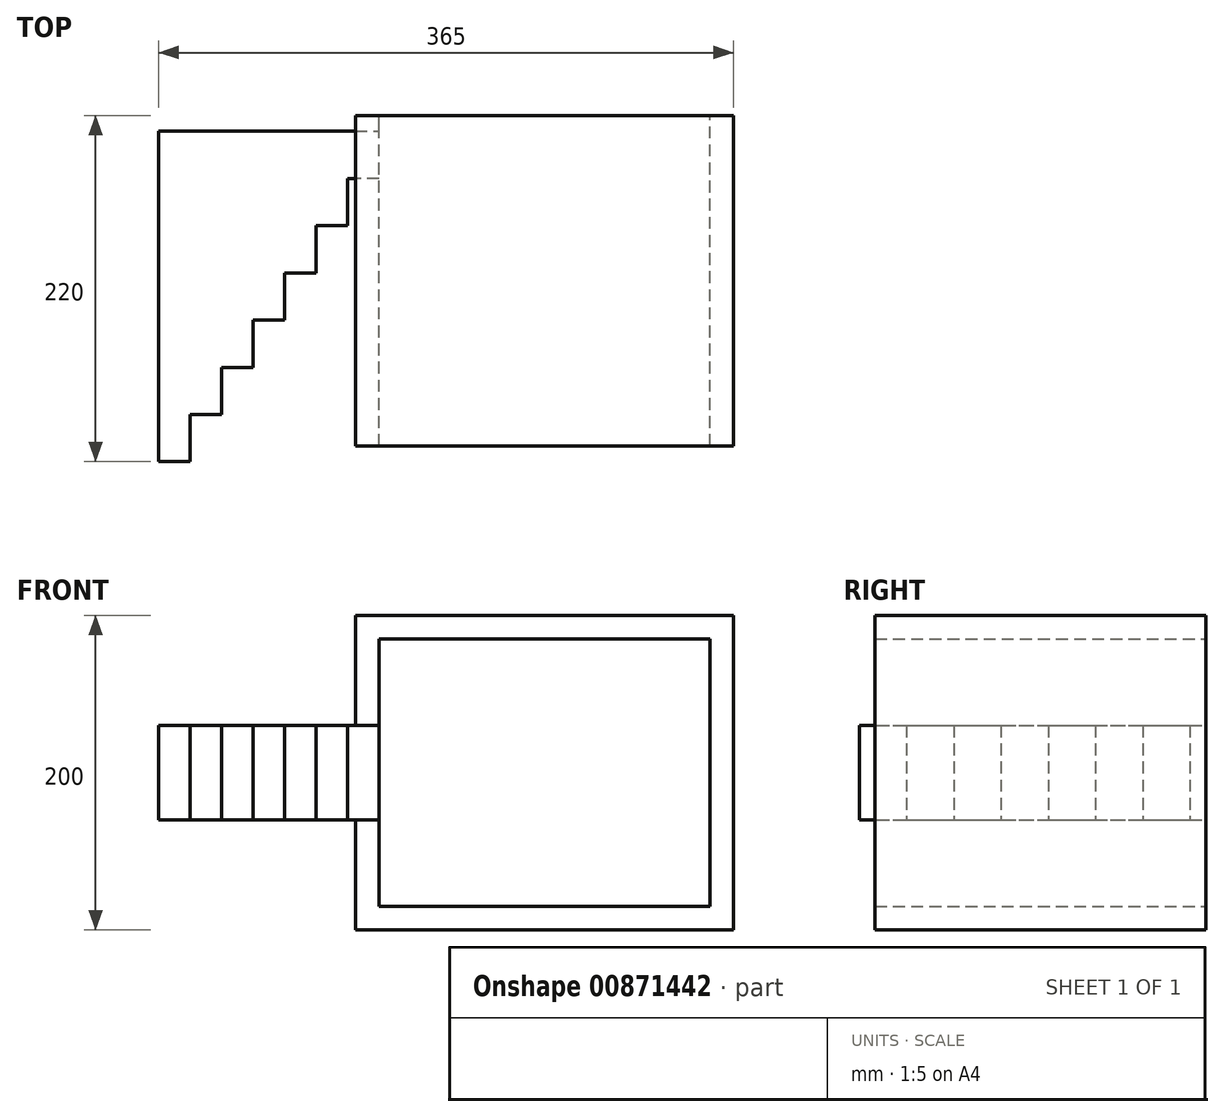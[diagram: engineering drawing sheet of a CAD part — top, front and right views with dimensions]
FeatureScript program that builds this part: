
annotation { "Feature Type Name" : "Feature", "Feature Type Description" : "" }
export const myFeature = defineFeature(function(context is Context, id is Id, definition is map)
    precondition{}
    {
        {
            var Q0;
            Q0=qCreatedBy(makeId("Front.planeOp"),FACE);
            var sketch = newSketch(context, id + "F0", { "sketchPlane" : qUnion([Q0])});
            skLineSegment(sketch, "E0.bottom", {"start": v(-120, 100) * mm, "end": v(120, 100) * mm});
            skLineSegment(sketch, "E0.top", {"start": v(-120, -100) * mm, "end": v(120, -100) * mm});
            skLineSegment(sketch, "E0.left", {"start": v(-120, 100) * mm, "end": v(-120, 30) * mm});
            skLineSegment(sketch, "E0.right", {"start": v(120, 100) * mm, "end": v(120, -100) * mm});
            skPoint(sketch, "E0.middle", {"position": v(0, 0) * mm});
            skLineSegment(sketch, "E1.bottom", {"start": v(-105, 85) * mm, "end": v(105, 85) * mm});
            skLineSegment(sketch, "E1.top", {"start": v(-105, -85) * mm, "end": v(105, -85) * mm});
            skLineSegment(sketch, "E1.left", {"start": v(-105, 85) * mm, "end": v(-105, -85) * mm});
            skLineSegment(sketch, "E1.right", {"start": v(105, 85) * mm, "end": v(105, -85) * mm});
            skLineSegment(sketch, "E2.bottom", {"start": v(-120, 30) * mm, "end": v(-265, 30) * mm});
            skLineSegment(sketch, "E2.top", {"start": v(-120, -30) * mm, "end": v(-265, -30) * mm});
            skLineSegment(sketch, "E2.right", {"start": v(-265, 30) * mm, "end": v(-265, -30) * mm});
            skLineSegment(sketch, "E3", {"start": v(-245, 30) * mm, "end": v(-245, -30) * mm});
            skLineSegment(sketch, "E4", {"start": v(-225, 30) * mm, "end": v(-225, -30) * mm});
            skLineSegment(sketch, "E5", {"start": v(-205, 30) * mm, "end": v(-205, -30) * mm});
            skLineSegment(sketch, "E6", {"start": v(-185, 30) * mm, "end": v(-185, -30) * mm});
            skLineSegment(sketch, "E7", {"start": v(-165, 30) * mm, "end": v(-165, -30) * mm});
            skLineSegment(sketch, "E8", {"start": v(-145, 30) * mm, "end": v(-145, -30) * mm});
            skLineSegment(sketch, "E9", {"start": v(-120, 30) * mm, "end": v(-105, 30) * mm});
            skLineSegment(sketch, "E10", {"start": v(-120, -30) * mm, "end": v(-105, -30) * mm});
            skLineSegment(sketch, "E11.trimOffspring", {"start": v(-120, -30) * mm, "end": v(-120, -100) * mm});
            skLineSegment(sketch, "E12", {"start": v(-125, 30) * mm, "end": v(-125, -30) * mm});
            skCircle(sketch, "E13", {"center": v(90, 70) * mm, "radius": 10 * mm});
            skSolve(sketch);
        }
        {
            var Q0;
            Q0=makeQuery(id+"F0.imprint","IMPRINT",FACE,{"disambiguationData":[TD([[makeQuery(id+"F0.imprint","IMPRINT",EDGE,{"derivedFrom":sQuery(id+"F0.wireOp",EDGE,"E0.bottom")}),-1.0]])]});
            extrude(context, id + "F1", {"entities" : qUnion([Q0]), "depth" : 200 * mm, "offsetDistance" : 25 * mm});
        }
        {
            var Q0;
            Q0=makeQuery(id+"F1.opExtrude","CAP_FACE",FACE,{"disambiguationData":[OSD([sQuery(id+"F0.wireOp",EDGE,"E0.bottom"),sQuery(id+"F0.wireOp",EDGE,"E0.top"),sQuery(id+"F0.wireOp",EDGE,"E0.left"),sQuery(id+"F0.wireOp",EDGE,"E0.right"),sQuery(id+"F0.wireOp",EDGE,"E1.bottom"),sQuery(id+"F0.wireOp",EDGE,"E1.top"),sQuery(id+"F0.wireOp",EDGE,"E1.left"),sQuery(id+"F0.wireOp",EDGE,"E1.right"),sQuery(id+"F0.wireOp",EDGE,"E9"),sQuery(id+"F0.wireOp",EDGE,"E10"),sQuery(id+"F0.wireOp",EDGE,"E11.trimOffspring")])],"isStart":true});
            extrude(context, id + "F2", {"entities" : qUnion([Q0]), "operationType" : NewBodyOperationType.ADD, "endBound" : BoundingType.SYMMETRIC, "depth" : 20 * mm, "offsetDistance" : 25 * mm});
        }
        {
            var Q0;
            {var subQ0=sQuery(id+"F0.wireOp",EDGE,"E9");Q0=makeQuery(id+"F0.imprint","IMPRINT",FACE,{"disambiguationData":[TD([[makeQuery(id+"F0.imprint","IMPRINT",EDGE,{"derivedFrom":subQ0}),-1.0]])]});}
            extrude(context, id + "F3", {"entities" : qUnion([Q0]), "operationType" : NewBodyOperationType.ADD, "depth" : 30 * mm, "offsetDistance" : 25 * mm});
        }
        {
            var Q0;
            {var subQ0=sQuery(id+"F0.wireOp",EDGE,"E8");Q0=makeQuery(id+"F0.imprint","IMPRINT",FACE,{"disambiguationData":[TD([[makeQuery(id+"F0.imprint","IMPRINT",EDGE,{"derivedFrom":subQ0}),1.0]])]});}
            extrude(context, id + "F4", {"entities" : qUnion([Q0]), "operationType" : NewBodyOperationType.ADD, "depth" : 60 * mm, "offsetDistance" : 25 * mm});
        }
        {
            var Q0;
            {var subQ0=sQuery(id+"F0.wireOp",EDGE,"E7");Q0=makeQuery(id+"F0.imprint","IMPRINT",FACE,{"disambiguationData":[TD([[makeQuery(id+"F0.imprint","IMPRINT",EDGE,{"derivedFrom":subQ0}),1.0]])]});}
            extrude(context, id + "F5", {"entities" : qUnion([Q0]), "operationType" : NewBodyOperationType.ADD, "depth" : 90 * mm, "offsetDistance" : 25 * mm});
        }
        {
            var Q0;
            {var subQ0=sQuery(id+"F0.wireOp",EDGE,"E6");Q0=makeQuery(id+"F0.imprint","IMPRINT",FACE,{"disambiguationData":[TD([[makeQuery(id+"F0.imprint","IMPRINT",EDGE,{"derivedFrom":subQ0}),1.0]])]});}
            extrude(context, id + "F6", {"entities" : qUnion([Q0]), "operationType" : NewBodyOperationType.ADD, "depth" : 120 * mm, "offsetDistance" : 25 * mm});
        }
        {
            var Q0;
            {var subQ0=sQuery(id+"F0.wireOp",EDGE,"E5");Q0=makeQuery(id+"F0.imprint","IMPRINT",FACE,{"disambiguationData":[TD([[makeQuery(id+"F0.imprint","IMPRINT",EDGE,{"derivedFrom":subQ0}),1.0]])]});}
            extrude(context, id + "F7", {"entities" : qUnion([Q0]), "operationType" : NewBodyOperationType.ADD, "depth" : 150 * mm, "offsetDistance" : 25 * mm});
        }
        {
            var Q0;
            {var subQ0=sQuery(id+"F0.wireOp",EDGE,"E4");Q0=makeQuery(id+"F0.imprint","IMPRINT",FACE,{"disambiguationData":[TD([[makeQuery(id+"F0.imprint","IMPRINT",EDGE,{"derivedFrom":subQ0}),1.0]])]});}
            extrude(context, id + "F8", {"entities" : qUnion([Q0]), "operationType" : NewBodyOperationType.ADD, "depth" : 180 * mm, "offsetDistance" : 25 * mm});
        }
        {
            var Q0;
            {var subQ0=sQuery(id+"F0.wireOp",EDGE,"E3");Q0=makeQuery(id+"F0.imprint","IMPRINT",FACE,{"disambiguationData":[TD([[makeQuery(id+"F0.imprint","IMPRINT",EDGE,{"derivedFrom":subQ0}),1.0]])]});}
            extrude(context, id + "F9", {"entities" : qUnion([Q0]), "operationType" : NewBodyOperationType.ADD, "depth" : 210 * mm, "offsetDistance" : 25 * mm});
        }
    });
